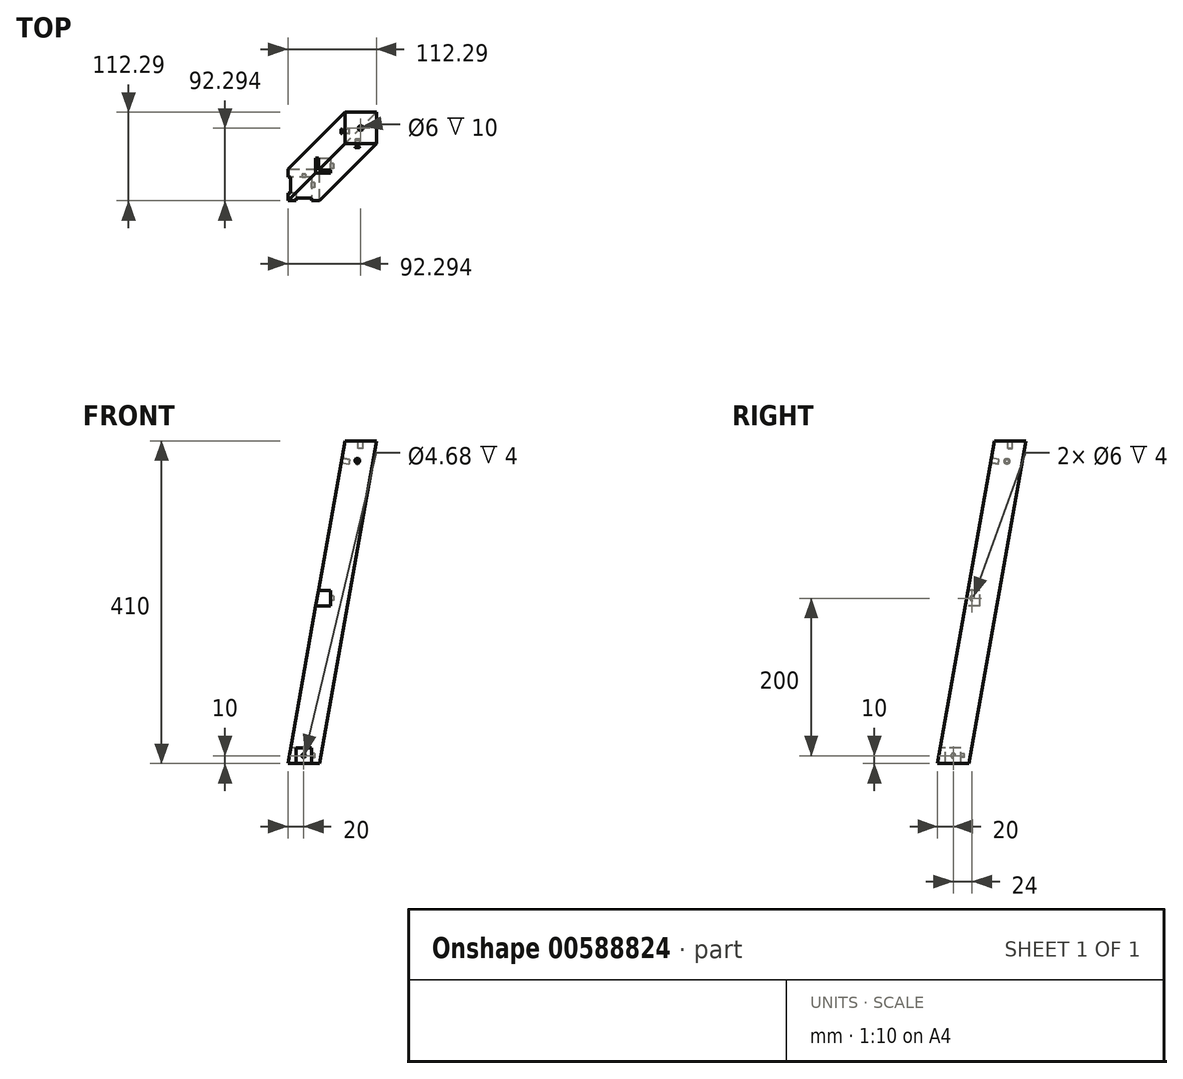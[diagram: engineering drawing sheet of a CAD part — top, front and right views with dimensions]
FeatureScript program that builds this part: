
annotation { "Feature Type Name" : "Feature", "Feature Type Description" : "" }
export const myFeature = defineFeature(function(context is Context, id is Id, definition is map)
    precondition{}
    {
        {
            var Q0;
            Q0=qCreatedBy(makeId("Top.planeOp"),FACE);
            var sketch = newSketch(context, id + "F0", { "sketchPlane" : qUnion([Q0])});
            skLineSegment(sketch, "E0.bottom", {"start": v(0, 0) * mm, "end": v(40, 0) * mm});
            skLineSegment(sketch, "E0.top", {"start": v(0, 40) * mm, "end": v(40, 40) * mm});
            skLineSegment(sketch, "E0.left", {"start": v(0, 0) * mm, "end": v(0, 40) * mm});
            skLineSegment(sketch, "E0.right", {"start": v(40, 0) * mm, "end": v(40, 40) * mm});
            skSolve(sketch);
        }
        {
            var Q0;
            Q0=qCreatedBy(makeId("Top.planeOp"),FACE);
            cPlane(context, id + "F1", {"entities" : qUnion([Q0]), "cplaneType" : CPlaneType.OFFSET, "offset" : 410 * mm, "width" : 150 * mm, "height" : 150 * mm});
        }
        {
            var Q0;
            Q0=qCreatedBy(id+"F1.planeOp",FACE);
            var sketch = newSketch(context, id + "F2", { "sketchPlane" : qUnion([Q0])});
            skLineSegment(sketch, "E1.bottom", {"start": v(72.3, 72.3) * mm, "end": v(112.3, 72.3) * mm});
            skLineSegment(sketch, "E1.top", {"start": v(72.3, 112.3) * mm, "end": v(112.3, 112.3) * mm});
            skLineSegment(sketch, "E1.left", {"start": v(72.3, 72.3) * mm, "end": v(72.3, 112.3) * mm});
            skLineSegment(sketch, "E1.right", {"start": v(112.3, 72.3) * mm, "end": v(112.3, 112.3) * mm});
            skSolve(sketch);
        }
        {
            var Q0;
            Q0=makeQuery(id+"F2.imprint","IMPRINT",FACE,{"disambiguationData":[TD([[makeQuery(id+"F2.imprint","IMPRINT",EDGE,{"derivedFrom":sQuery(id+"F2.wireOp",EDGE,"E1.bottom")}),1.0]])]});
            var Q1;
            Q1=makeQuery(id+"F0.imprint","IMPRINT",FACE,{"disambiguationData":[TD([[makeQuery(id+"F0.imprint","IMPRINT",EDGE,{"derivedFrom":sQuery(id+"F0.wireOp",EDGE,"E0.bottom")}),1.0]])]});
            loft(context, id + "F3", {"sheetProfilesArray" : [{ "sheetProfileEntities" : qUnion([Q0]) }, { "sheetProfileEntities" : qUnion([Q1]) }]});
        }
        {
            var Q0;
            Q0=qCreatedBy(makeId("Right.planeOp"),FACE);
            var sketch = newSketch(context, id + "F4", { "sketchPlane" : qUnion([Q0])});
            skLineSegment(sketch, "E2.bottom", {"start": v(30, 0) * mm, "end": v(10, 0) * mm});
            skLineSegment(sketch, "E2.top", {"start": v(30, 20) * mm, "end": v(10, 20) * mm});
            skLineSegment(sketch, "E2.left", {"start": v(30, 0) * mm, "end": v(30, 20) * mm});
            skLineSegment(sketch, "E2.right", {"start": v(10, 0) * mm, "end": v(10, 20) * mm});
            skSolve(sketch);
        }
        {
            var Q0;
            Q0=makeQuery(id+"F4.imprint","IMPRINT",FACE,{"disambiguationData":[TD([[makeQuery(id+"F4.imprint","IMPRINT",EDGE,{"derivedFrom":sQuery(id+"F4.wireOp",EDGE,"E2.bottom")}),-1.0]])]});
            extrude(context, id + "F5", {"entities" : qUnion([Q0]), "operationType" : NewBodyOperationType.REMOVE, "depth" : 30 * mm, "offsetDistance" : 25 * mm});
        }
        {
            var Q0;
            Q0=qCreatedBy(makeId("Front.planeOp"),FACE);
            var sketch = newSketch(context, id + "F6", { "sketchPlane" : qUnion([Q0])});
            skLineSegment(sketch, "E3.bottom", {"start": v(10, 0) * mm, "end": v(30, 0) * mm});
            skLineSegment(sketch, "E3.top", {"start": v(10, 20) * mm, "end": v(30, 20) * mm});
            skLineSegment(sketch, "E3.left", {"start": v(10, 0) * mm, "end": v(10, 20) * mm});
            skLineSegment(sketch, "E3.right", {"start": v(30, 0) * mm, "end": v(30, 20) * mm});
            skSolve(sketch);
        }
        {
            var Q0;
            Q0=makeQuery(id+"F6.imprint","IMPRINT",FACE,{"disambiguationData":[TD([[makeQuery(id+"F6.imprint","IMPRINT",EDGE,{"derivedFrom":sQuery(id+"F6.wireOp",EDGE,"E3.bottom")}),1.0]])]});
            extrude(context, id + "F7", {"entities" : qUnion([Q0]), "operationType" : NewBodyOperationType.REMOVE, "oppositeDirection" : true, "depth" : 30 * mm, "offsetDistance" : 25 * mm});
        }
        {
            var Q0;
            Q0=makeQuery(id+"F3.opLoft","SWEPT_FACE",FACE,{"disambiguationData":[OSD([sQuery(id+"F0.wireOp",EDGE,"E0.bottom"),sQuery(id+"F0.wireOp",EDGE,"E0.left"),sQuery(id+"F0.wireOp",EDGE,"E0.right"),sQuery(id+"F2.wireOp",EDGE,"E1.bottom"),sQuery(id+"F2.wireOp",EDGE,"E1.left"),sQuery(id+"F2.wireOp",EDGE,"E1.right")])]});
            var sketch = newSketch(context, id + "F8", { "sketchPlane" : qUnion([Q0])});
            skCircle(sketch, "E4", {"center": v(88.17, 390.82) * mm, "radius": 3 * mm});
            skSolve(sketch);
        }
        {
            var Q0;
            Q0=makeQuery(id+"F8.imprint","IMPRINT",FACE,{"disambiguationData":[TD([[makeQuery(id+"F8.imprint","IMPRINT",EDGE,{"derivedFrom":sQuery(id+"F8.wireOp",EDGE,"E4")}),1.0]])]});
            extrude(context, id + "F9", {"entities" : qUnion([Q0]), "operationType" : NewBodyOperationType.REMOVE, "oppositeDirection" : true, "depth" : 10 * mm, "offsetDistance" : 25 * mm});
        }
        {
            var Q0;
            Q0=makeQuery(id+"F3.opLoft","SWEPT_FACE",FACE,{"disambiguationData":[OSD([sQuery(id+"F0.wireOp",EDGE,"E0.bottom"),sQuery(id+"F0.wireOp",EDGE,"E0.top"),sQuery(id+"F0.wireOp",EDGE,"E0.left"),sQuery(id+"F2.wireOp",EDGE,"E1.bottom"),sQuery(id+"F2.wireOp",EDGE,"E1.top"),sQuery(id+"F2.wireOp",EDGE,"E1.left")])]});
            var sketch = newSketch(context, id + "F10", { "sketchPlane" : qUnion([Q0])});
            skCircle(sketch, "E5", {"center": v(-88.17, 390.82) * mm, "radius": 3 * mm});
            skSolve(sketch);
        }
        {
            var Q0;
            Q0=makeQuery(id+"F10.imprint","IMPRINT",FACE,{"disambiguationData":[TD([[makeQuery(id+"F10.imprint","IMPRINT",EDGE,{"derivedFrom":sQuery(id+"F10.wireOp",EDGE,"E5")}),1.0]])]});
            extrude(context, id + "F11", {"entities" : qUnion([Q0]), "operationType" : NewBodyOperationType.REMOVE, "oppositeDirection" : true, "depth" : 10 * mm, "offsetDistance" : 25 * mm});
        }
        {
            var Q0;
            Q0=makeQuery(id+"F7.boolean.opBoolean","MERGE",FACE,{"derivedFrom":[makeQuery(id+"F5.boolean.opBoolean","COPY",FACE,{"derivedFrom":makeQuery(id+"F5.opExtrude","CAP_FACE",FACE,{"disambiguationData":[OSD([sQuery(id+"F4.wireOp",EDGE,"E2.bottom"),sQuery(id+"F4.wireOp",EDGE,"E2.top"),sQuery(id+"F4.wireOp",EDGE,"E2.left"),sQuery(id+"F4.wireOp",EDGE,"E2.right")])],"isStart":false})}),makeQuery(id+"F7.opExtrude","SWEPT_FACE",FACE,{"disambiguationData":[OSD([sQuery(id+"F6.wireOp",EDGE,"E3.right")])]})]});
            var sketch = newSketch(context, id + "F12", { "sketchPlane" : qUnion([Q0])});
            skCircle(sketch, "E6", {"center": v(-20, 10) * mm, "radius": 3 * mm});
            skSolve(sketch);
        }
        {
            var Q0;
            Q0 = qSketchRegion(id + "F12", true);
            extrude(context, id + "F13", {"entities" : qUnion([Q0]), "operationType" : NewBodyOperationType.REMOVE, "oppositeDirection" : true, "depth" : 4 * mm, "offsetDistance" : 25 * mm});
        }
        {
            var Q0;
            Q0=makeQuery(id+"F5.boolean.opBoolean","COPY",FACE,{"derivedFrom":makeQuery(id+"F5.opExtrude","SWEPT_FACE",FACE,{"disambiguationData":[OSD([sQuery(id+"F4.wireOp",EDGE,"E2.left")])]})});
            var sketch = newSketch(context, id + "F14", { "sketchPlane" : qUnion([Q0])});
            skCircle(sketch, "E7", {"center": v(20, 10) * mm, "radius": 2.34 * mm});
            skSolve(sketch);
        }
        {
            var Q0;
            Q0=makeQuery(id+"F14.imprint","IMPRINT",FACE,{"disambiguationData":[TD([[makeQuery(id+"F14.imprint","IMPRINT",EDGE,{"derivedFrom":sQuery(id+"F14.wireOp",EDGE,"E7")}),1.0]])]});
            extrude(context, id + "F15", {"entities" : qUnion([Q0]), "operationType" : NewBodyOperationType.REMOVE, "oppositeDirection" : true, "depth" : 4 * mm, "offsetDistance" : 25 * mm});
        }
        {
            var Q0;
            Q0=qCreatedBy(makeId("Front.planeOp"),FACE);
            var sketch = newSketch(context, id + "F16", { "sketchPlane" : qUnion([Q0])});
            skLineSegment(sketch, "E8.bottom", {"start": v(34.94, 200) * mm, "end": v(53.94, 200) * mm});
            skLineSegment(sketch, "E8.top", {"start": v(34.94, 220) * mm, "end": v(53.94, 220) * mm});
            skLineSegment(sketch, "E8.left", {"start": v(34.94, 200) * mm, "end": v(34.94, 220) * mm});
            skLineSegment(sketch, "E8.right", {"start": v(53.94, 200) * mm, "end": v(53.94, 220) * mm});
            skSolve(sketch);
        }
        {
            var Q0;
            Q0=makeQuery(id+"F16.imprint","IMPRINT",FACE,{"disambiguationData":[TD([[makeQuery(id+"F16.imprint","IMPRINT",EDGE,{"derivedFrom":sQuery(id+"F16.wireOp",EDGE,"E8.bottom")}),1.0]])]});
            extrude(context, id + "F17", {"entities" : qUnion([Q0]), "operationType" : NewBodyOperationType.REMOVE, "oppositeDirection" : true, "depth" : 54 * mm, "offsetDistance" : 25 * mm});
        }
        {
            var Q0;
            Q0=makeQuery(id+"F17.boolean.opBoolean","COPY",FACE,{"derivedFrom":makeQuery(id+"F17.opExtrude","SWEPT_FACE",FACE,{"disambiguationData":[OSD([sQuery(id+"F16.wireOp",EDGE,"E8.right")])]})});
            var sketch = newSketch(context, id + "F18", { "sketchPlane" : qUnion([Q0])});
            skCircle(sketch, "E9", {"center": v(-44, 210) * mm, "radius": 3 * mm});
            skSolve(sketch);
        }
        {
            var Q0;
            Q0=makeQuery(id+"F18.imprint","IMPRINT",FACE,{"disambiguationData":[TD([[makeQuery(id+"F18.imprint","IMPRINT",EDGE,{"derivedFrom":sQuery(id+"F18.wireOp",EDGE,"E9")}),1.0]])]});
            extrude(context, id + "F19", {"entities" : qUnion([Q0]), "operationType" : NewBodyOperationType.REMOVE, "oppositeDirection" : true, "depth" : 4 * mm, "offsetDistance" : 25 * mm});
        }
        {
            var Q0;
            Q0=makeQuery(id+"F3.opLoft","CAP_FACE",FACE,{"disambiguationData":[OSD([makeQuery(id+"F2.imprint","IMPRINT",FACE,{"disambiguationData":[TD([[makeQuery(id+"F2.imprint","IMPRINT",EDGE,{"derivedFrom":sQuery(id+"F2.wireOp",EDGE,"E1.bottom")}),1.0]])]})])],"isStart":true});
            var sketch = newSketch(context, id + "F20", { "sketchPlane" : qUnion([Q0])});
            skCircle(sketch, "E10", {"center": v(92.3, 92.3) * mm, "radius": 3 * mm});
            skSolve(sketch);
        }
        {
            var Q0;
            Q0=makeQuery(id+"F20.imprint","IMPRINT",FACE,{"disambiguationData":[TD([[makeQuery(id+"F20.imprint","IMPRINT",EDGE,{"derivedFrom":sQuery(id+"F20.wireOp",EDGE,"E10")}),1.0]])]});
            extrude(context, id + "F21", {"entities" : qUnion([Q0]), "operationType" : NewBodyOperationType.REMOVE, "oppositeDirection" : true, "depth" : 10 * mm, "offsetDistance" : 25 * mm});
        }
    });
